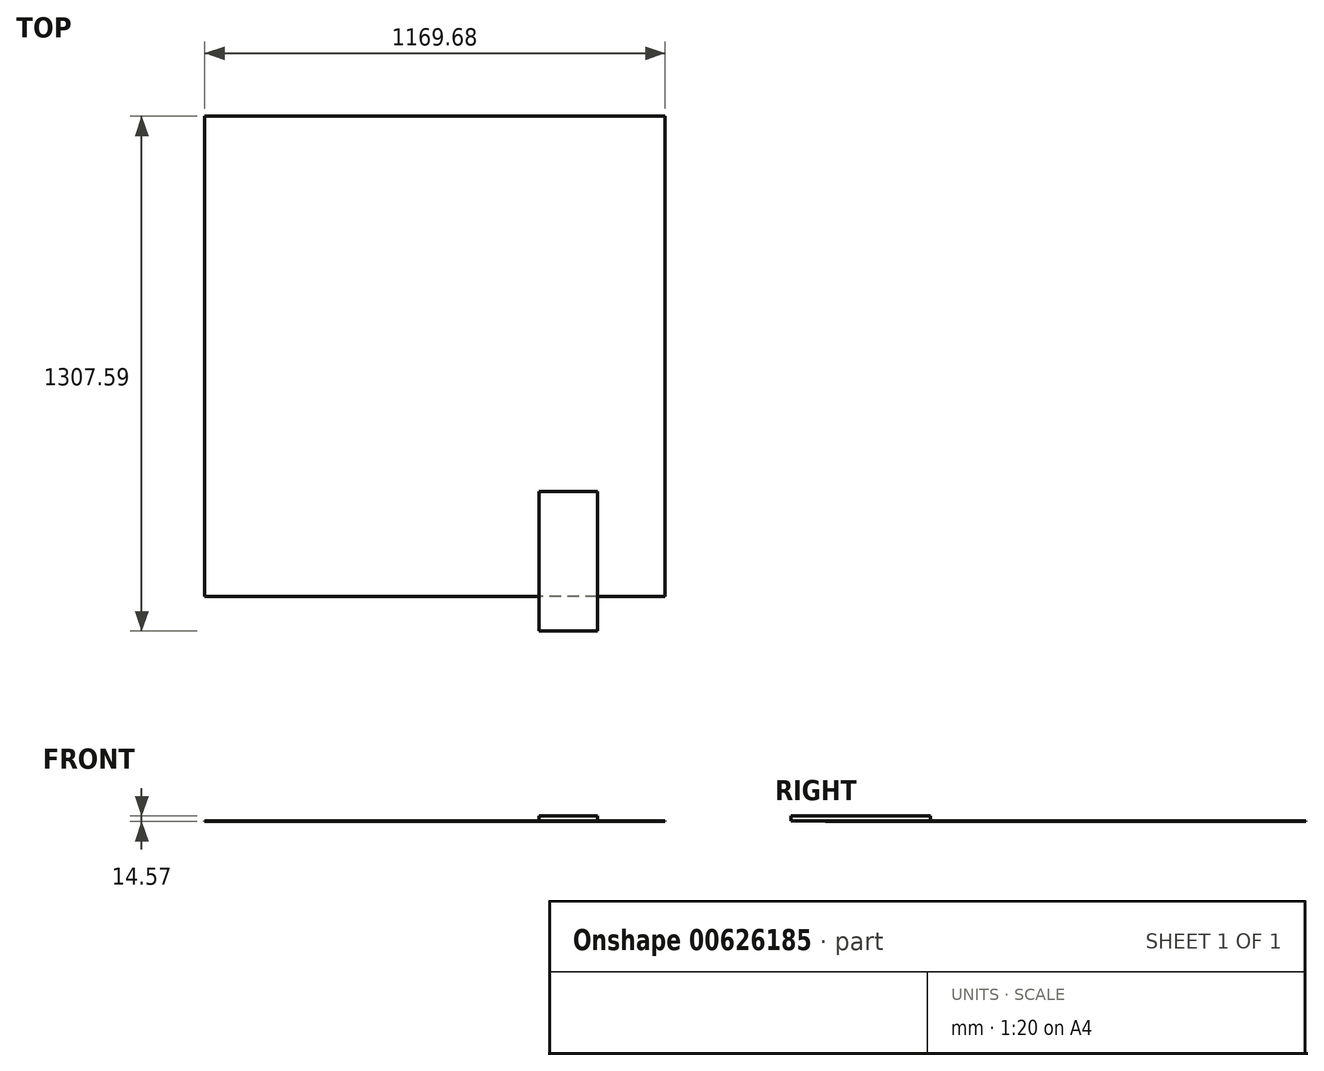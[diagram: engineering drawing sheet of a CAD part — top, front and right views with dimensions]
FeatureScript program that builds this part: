
annotation { "Feature Type Name" : "Feature", "Feature Type Description" : "" }
export const myFeature = defineFeature(function(context is Context, id is Id, definition is map)
    precondition{}
    {
        {
            var Q0;
            Q0=qCreatedBy(makeId("Top.planeOp"),FACE);
            var sketch = newSketch(context, id + "F0", { "sketchPlane" : qUnion([Q0])});
            skLineSegment(sketch, "E0.bottom", {"start": v(584.84, 609.98) * mm, "end": v(-584.83, 609.98) * mm});
            skLineSegment(sketch, "E0.top", {"start": v(584.84, -609.98) * mm, "end": v(-584.84, -609.98) * mm});
            skLineSegment(sketch, "E0.left", {"start": v(584.84, 609.98) * mm, "end": v(584.84, -609.98) * mm});
            skLineSegment(sketch, "E0.right", {"start": v(-584.83, 609.98) * mm, "end": v(-584.84, -609.98) * mm});
            skPoint(sketch, "E0.middle", {"position": v(0, 0) * mm});
            skSolve(sketch);
        }
        {
            var Q0;
            Q0=makeQuery(id+"F0.imprint","IMPRINT",FACE,{"disambiguationData":[TD([[makeQuery(id+"F0.imprint","IMPRINT",EDGE,{"derivedFrom":sQuery(id+"F0.wireOp",EDGE,"E0.bottom")}),1.0]])]});
            extrude(context, id + "F1", {"entities" : qUnion([Q0]), "depth" : 1.56 * mm, "offsetDistance" : 25.4 * mm});
        }
        {
            var Q0;
            Q0=makeQuery(id+"F1.opExtrude","CAP_FACE",FACE,{"disambiguationData":[OSD([sQuery(id+"F0.wireOp",EDGE,"E0.bottom"),sQuery(id+"F0.wireOp",EDGE,"E0.top"),sQuery(id+"F0.wireOp",EDGE,"E0.left"),sQuery(id+"F0.wireOp",EDGE,"E0.right")])],"isStart":false});
            var sketch = newSketch(context, id + "F2", { "sketchPlane" : qUnion([Q0])});
            skLineSegment(sketch, "E1", {"start": v(412.37, -343.79) * mm, "end": v(264.03, -343.79) * mm});
            skLineSegment(sketch, "E2", {"start": v(264.03, -343.79) * mm, "end": v(264.03, -697.61) * mm});
            skLineSegment(sketch, "E3", {"start": v(264.03, -697.61) * mm, "end": v(412.37, -697.61) * mm});
            skLineSegment(sketch, "E4", {"start": v(412.37, -343.79) * mm, "end": v(412.37, -697.61) * mm});
            skSolve(sketch);
        }
        {
            var Q0;
            Q0 = qSketchRegion(id + "F2", true);
            extrude(context, id + "F3", {"entities" : qUnion([Q0]), "operationType" : NewBodyOperationType.ADD, "depth" : 13 * mm, "offsetDistance" : 25.4 * mm});
        }
    });
